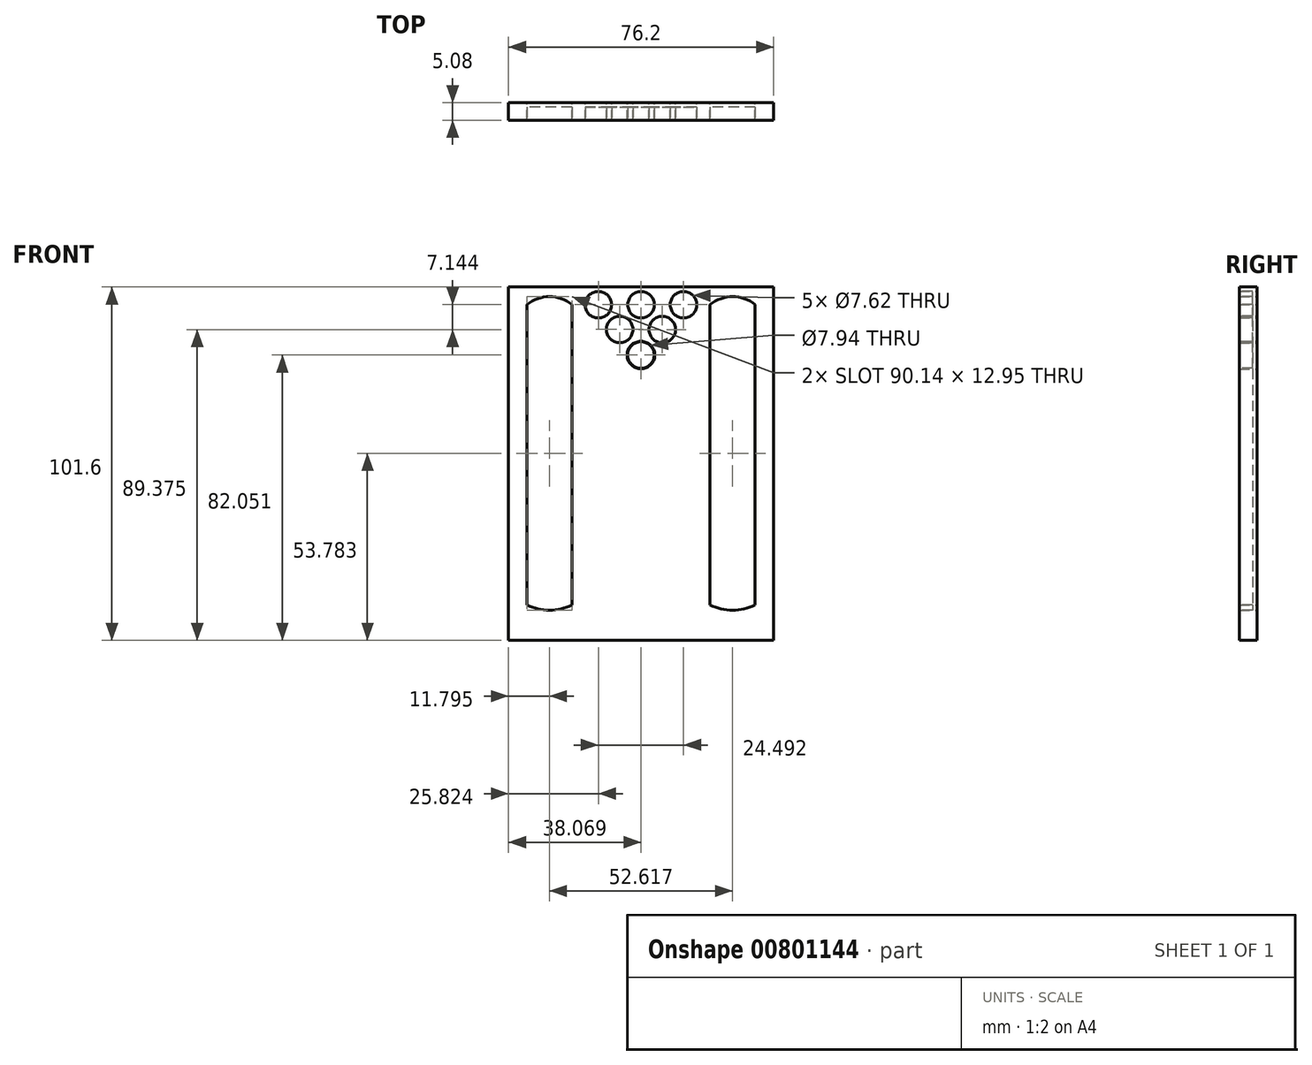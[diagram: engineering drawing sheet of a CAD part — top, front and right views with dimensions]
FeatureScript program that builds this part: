
annotation { "Feature Type Name" : "Feature", "Feature Type Description" : "" }
export const myFeature = defineFeature(function(context is Context, id is Id, definition is map)
    precondition{}
    {
        {
            var Q0;
            Q0=qCreatedBy(makeId("Front.planeOp"),FACE);
            var sketch = newSketch(context, id + "F0", { "sketchPlane" : qUnion([Q0])});
            skLineSegment(sketch, "E0", {"start": v(-41.28, 43.09) * mm, "end": v(34.92, 43.09) * mm});
            skLineSegment(sketch, "E1", {"start": v(34.92, 43.09) * mm, "end": v(34.92, -58.51) * mm});
            skLineSegment(sketch, "E2", {"start": v(34.92, -58.51) * mm, "end": v(-41.28, -58.51) * mm});
            skLineSegment(sketch, "E3", {"start": v(-41.28, -58.51) * mm, "end": v(-41.28, 43.09) * mm});
            skLineSegment(sketch, "E4", {"start": v(-35.96, 38) * mm, "end": v(-35.96, -48.35) * mm});
            skArc(sketch, "E5", {"start": v(-35.96, -48.35) * mm, "mid": v(-29.48, -49.8) * mm, "end": v(-23, -48.35) * mm});
            skLineSegment(sketch, "E6.trimOffspring", {"start": v(-23.26, 38) * mm, "end": v(-19.27, 38) * mm});
            skArc(sketch, "E7", {"start": v(-23, 38) * mm, "mid": v(-29.48, 40.34) * mm, "end": v(-35.96, 38) * mm});
            skLineSegment(sketch, "E8", {"start": v(-23, 38) * mm, "end": v(-23, -48.35) * mm});
            skLineSegment(sketch, "E9", {"start": v(29.6, 38) * mm, "end": v(29.6, -48.35) * mm});
            skArc(sketch, "E10", {"start": v(29.6, 38) * mm, "mid": v(23.13, 40.34) * mm, "end": v(16.66, 38) * mm});
            skArc(sketch, "E11", {"start": v(16.66, -48.35) * mm, "mid": v(23.13, -49.8) * mm, "end": v(29.6, -48.35) * mm});
            skLineSegment(sketch, "E12", {"start": v(16.66, 38) * mm, "end": v(16.66, -48.35) * mm});
            skCircle(sketch, "E13", {"center": v(-15.46, 38) * mm, "radius": 3.81 * mm});
            skCircle(sketch, "E14", {"center": v(9.04, 38) * mm, "radius": 3.81 * mm});
            skCircle(sketch, "E15", {"center": v(-9.32, 30.9) * mm, "radius": 3.81 * mm});
            skCircle(sketch, "E16", {"center": v(2.93, 30.87) * mm, "radius": 3.81 * mm});
            skCircle(sketch, "E17", {"center": v(-3.21, 23.54) * mm, "radius": 3.97 * mm});
            skLineSegment(sketch, "E18.trimOffspring", {"start": v(16.66, 38) * mm, "end": v(34.92, 38) * mm});
            skLineSegment(sketch, "E19", {"start": v(-23, 38) * mm, "end": v(16.66, 38) * mm});
            skCircle(sketch, "E20", {"center": v(-3.18, 38) * mm, "radius": 3.81 * mm});
            skSolve(sketch);
        }
        {
            var Q0;
            Q0=sQuery(id+"F0.wireOp",EDGE,"E13");
            var Q1;
            Q1=sQuery(id+"F0.wireOp",EDGE,"E20");
            var Q2;
            Q2=sQuery(id+"F0.wireOp",EDGE,"E14");
            var Q3;
            Q3=sQuery(id+"F0.wireOp",EDGE,"E16");
            var Q4;
            Q4=sQuery(id+"F0.wireOp",EDGE,"E17");
            var Q5;
            Q5=sQuery(id+"F0.wireOp",EDGE,"E15");
            extrude(context, id + "F1", {"bodyType" : ToolBodyType.SURFACE, "surfaceEntities" : qUnion([Q0, Q1, Q2, Q3, Q4, Q5]), "depth" : 5.08 * mm, "offsetDistance" : 25.4 * mm});
        }
        {
            var Q0;
            Q0 = qSketchRegion(id + "F0", true);
            extrude(context, id + "F2", {"entities" : qUnion([Q0]), "depth" : 5.08 * mm, "offsetDistance" : 25.4 * mm});
        }
        {
            var Q0;
            Q0=makeQuery(id+"F2.opExtrude","CAP_FACE",FACE,{"disambiguationData":[OSD([sQuery(id+"F0.wireOp",EDGE,"E0"),sQuery(id+"F0.wireOp",EDGE,"E1"),sQuery(id+"F0.wireOp",EDGE,"E2"),sQuery(id+"F0.wireOp",EDGE,"E3"),sQuery(id+"F0.wireOp",EDGE,"E4"),sQuery(id+"F0.wireOp",EDGE,"E5"),sQuery(id+"F0.wireOp",EDGE,"E7"),sQuery(id+"F0.wireOp",EDGE,"E8"),sQuery(id+"F0.wireOp",EDGE,"E9"),sQuery(id+"F0.wireOp",EDGE,"E10"),sQuery(id+"F0.wireOp",EDGE,"E11"),sQuery(id+"F0.wireOp",EDGE,"E12"),sQuery(id+"F0.wireOp",EDGE,"E13"),sQuery(id+"F0.wireOp",EDGE,"E14"),sQuery(id+"F0.wireOp",EDGE,"E15"),sQuery(id+"F0.wireOp",EDGE,"E16"),sQuery(id+"F0.wireOp",EDGE,"E17"),sQuery(id+"F0.wireOp",EDGE,"E20")])],"isStart":false});
            var sketch = newSketch(context, id + "F3", { "sketchPlane" : qUnion([Q0])});
            skCircle(sketch, "E21", {"center": v(-15.46, 38) * mm, "radius": 3.81 * mm});
            skCircle(sketch, "E22", {"center": v(-3.18, 38) * mm, "radius": 3.81 * mm});
            skCircle(sketch, "E23", {"center": v(9.04, 38) * mm, "radius": 3.81 * mm});
            skCircle(sketch, "E24", {"center": v(2.93, 30.87) * mm, "radius": 3.81 * mm});
            skCircle(sketch, "E25", {"center": v(-9.32, 30.9) * mm, "radius": 3.81 * mm});
            skCircle(sketch, "E26", {"center": v(-3.21, 23.54) * mm, "radius": 3.81 * mm});
            skArc(sketch, "E27", {"start": v(-23, 38) * mm, "mid": v(-29.48, 40.3) * mm, "end": v(-35.96, 38) * mm});
            skLineSegment(sketch, "E28", {"start": v(-35.96, 38) * mm, "end": v(-35.96, -48.35) * mm});
            skLineSegment(sketch, "E29", {"start": v(-23, 38) * mm, "end": v(-23, -48.35) * mm});
            skArc(sketch, "E30", {"start": v(-35.96, -48.35) * mm, "mid": v(-29.48, -49.8) * mm, "end": v(-23, -48.35) * mm});
            skArc(sketch, "E31", {"start": v(29.6, 38) * mm, "mid": v(23.13, 40.34) * mm, "end": v(16.66, 38) * mm});
            skLineSegment(sketch, "E32", {"start": v(16.66, 38) * mm, "end": v(16.66, -48.35) * mm});
            skLineSegment(sketch, "E33", {"start": v(29.6, 38) * mm, "end": v(29.6, -48.35) * mm});
            skArc(sketch, "E34", {"start": v(16.66, -48.35) * mm, "mid": v(23.13, -49.8) * mm, "end": v(29.6, -48.35) * mm});
            skArc(sketch, "E35", {"start": v(-23, 38) * mm, "mid": v(-29.48, 40.34) * mm, "end": v(-35.96, 38) * mm});
            skSolve(sketch);
        }
        {
            var Q0;
            Q0 = qSketchRegion(id + "F3", true);
            extrude(context, id + "F4", {"entities" : qUnion([Q0]), "oppositeDirection" : true, "depth" : 3.8 * mm, "offsetDistance" : 25.4 * mm});
        }
    });
